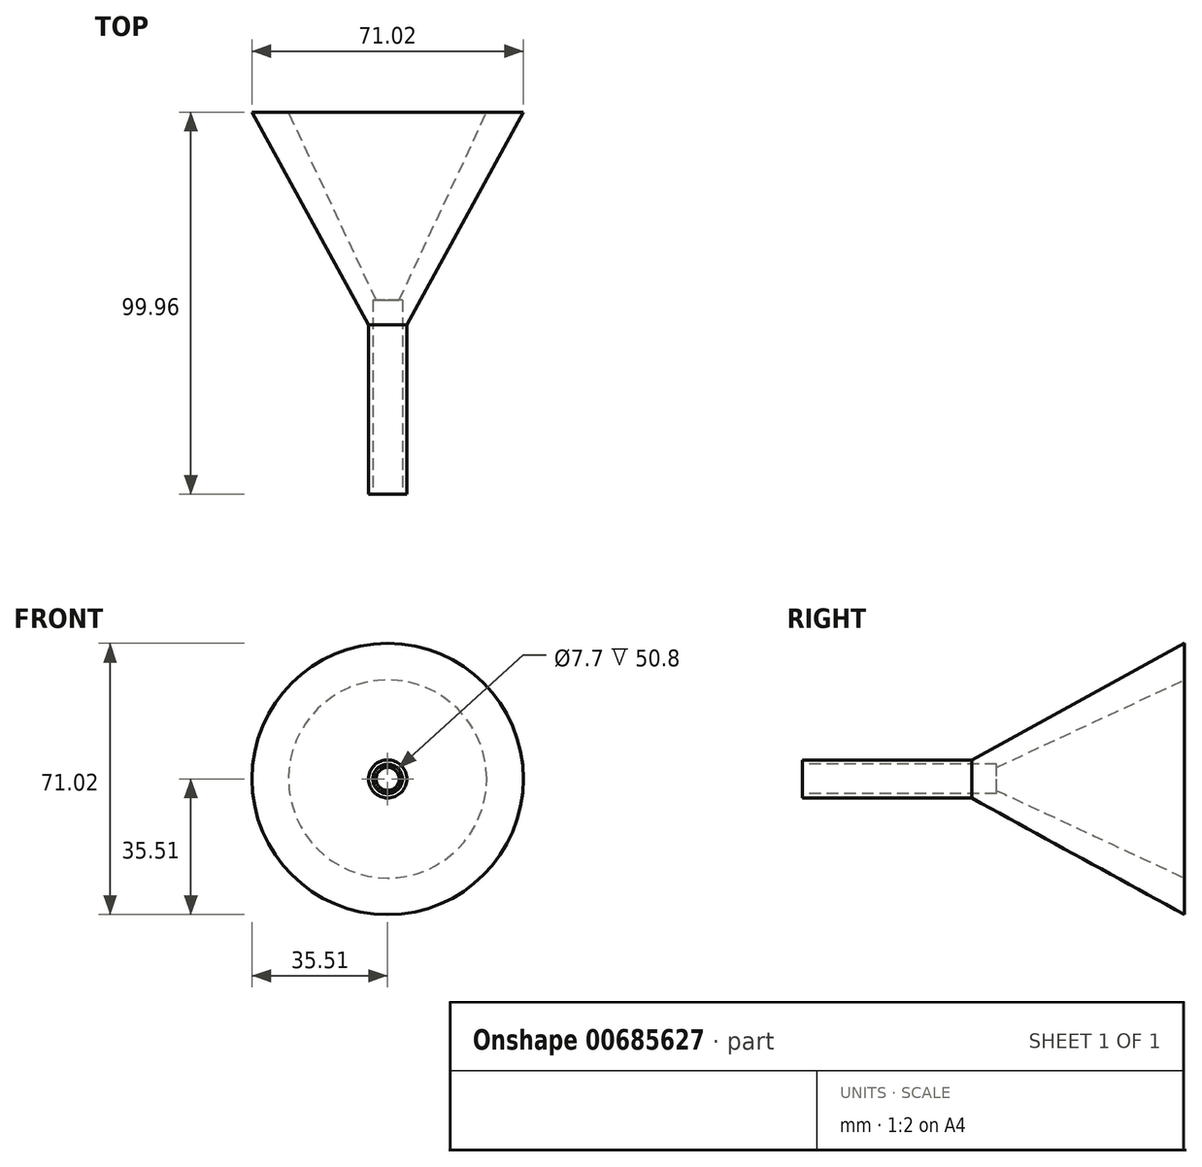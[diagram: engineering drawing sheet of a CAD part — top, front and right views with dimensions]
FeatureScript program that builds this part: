
annotation { "Feature Type Name" : "Feature", "Feature Type Description" : "" }
export const myFeature = defineFeature(function(context is Context, id is Id, definition is map)
    precondition{}
    {
        {
            var Q0;
            Q0=qCreatedBy(makeId("Top.planeOp"),FACE);
            var sketch = newSketch(context, id + "F0", { "sketchPlane" : qUnion([Q0])});
            skLineSegment(sketch, "E0", {"start": v(25.92, 55.65) * mm, "end": v(35.5, 55.65) * mm});
            skLineSegment(sketch, "E1", {"start": v(35.5, 55.65) * mm, "end": v(4.99, 0) * mm});
            skLineSegment(sketch, "E2", {"start": v(4.99, 0) * mm, "end": v(4.99, -44.3) * mm});
            skLineSegment(sketch, "E3", {"start": v(4.99, -44.3) * mm, "end": v(0, -44.3) * mm});
            skLineSegment(sketch, "E4", {"start": v(0, -44.3) * mm, "end": v(0, 0) * mm});
            skLineSegment(sketch, "E5", {"start": v(0, 0) * mm, "end": v(25.92, 55.65) * mm});
            skSolve(sketch);
        }
        {
            var Q0;
            Q0 = qSketchRegion(id + "F0", true);
            var Q1;
            Q1=sQuery(id+"F0.wireOp",EDGE,"E4");
            revolve(context, id + "F1", {"surfaceOperationType" : NewSurfaceOperationType.NEW, "entities" : qUnion([Q0]), "axis" : qUnion([Q1]), "revolveType" : RevolveType.FULL});
        }
        {
            var Q0;
            Q0=makeQuery(id+"F1.opRevolve","SWEPT_FACE",FACE,{"disambiguationData":[OSD([sQuery(id+"F0.wireOp",EDGE,"E3")])]});
            var sketch = newSketch(context, id + "F2", { "sketchPlane" : qUnion([Q0])});
            skCircle(sketch, "E6", {"center": v(0, 0) * mm, "radius": 3.85 * mm});
            skSolve(sketch);
        }
        {
            var Q0;
            Q0=makeQuery(id+"F2.imprint","IMPRINT",FACE,{"disambiguationData":[TD([[makeQuery(id+"F2.imprint","IMPRINT",EDGE,{"derivedFrom":sQuery(id+"F2.wireOp",EDGE,"E6")}),1.0]])]});
            extrude(context, id + "F3", {"entities" : qUnion([Q0]), "operationType" : NewBodyOperationType.REMOVE, "oppositeDirection" : true, "depth" : 50.8 * mm, "offsetDistance" : 25.4 * mm});
        }
    });
